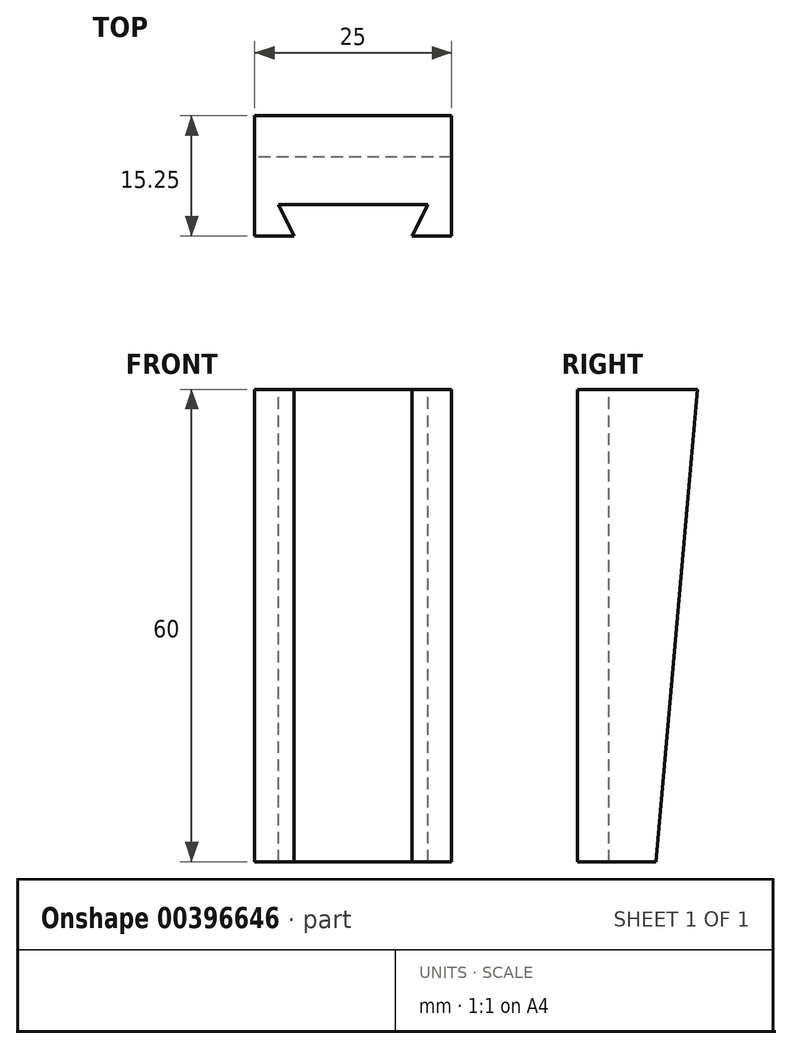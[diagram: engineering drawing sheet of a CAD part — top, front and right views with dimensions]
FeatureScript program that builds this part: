
annotation { "Feature Type Name" : "Feature", "Feature Type Description" : "" }
export const myFeature = defineFeature(function(context is Context, id is Id, definition is map)
    precondition{}
    {
        {
            assignVariable(context, id + "F0", {"name" : "height", "anyValue" : 60});
        }
        {
            assignVariable(context, id + "F1", {"name" : "width", "anyValue" : 25});
        }
        {
            var Q0;
            Q0=qCreatedBy(makeId("Top.planeOp"),FACE);
            var sketch = newSketch(context, id + "F2", { "sketchPlane" : qUnion([Q0])});
            skLineSegment(sketch, "E0.bottom", {"start": v(12.5, 10) * mm, "end": v(-12.5, 10) * mm});
            skLineSegment(sketch, "E0.top", {"start": v(12.5, 0) * mm, "end": v(-12.5, 0) * mm});
            skLineSegment(sketch, "E0.left", {"start": v(12.5, 10) * mm, "end": v(12.5, 0) * mm});
            skLineSegment(sketch, "E0.right", {"start": v(-12.5, 10) * mm, "end": v(-12.5, 0) * mm});
            skSolve(sketch);
        }
        {
            var Q0;
            Q0=makeQuery(id+"F2.imprint","IMPRINT",FACE,{"disambiguationData":[TD([[makeQuery(id+"F2.imprint","IMPRINT",EDGE,{"derivedFrom":sQuery(id+"F2.wireOp",EDGE,"E0.bottom")}),1.0]])]});
            extrude(context, id + "F3", {"entities" : qUnion([Q0]), "depth" : (getVariable(context, 'height')) * mm});
        }
        {
            var Q0;
            Q0=qCreatedBy(makeId("Right.planeOp"),FACE);
            var sketch = newSketch(context, id + "F4", { "sketchPlane" : qUnion([Q0])});
            skLineSegment(sketch, "E1", {"start": v(10, 0) * mm, "end": v(10, 60) * mm});
            skLineSegment(sketch, "E2", {"start": v(10, 60) * mm, "end": v(15.25, 60) * mm});
            skLineSegment(sketch, "E3", {"start": v(15.25, 60) * mm, "end": v(10, 0) * mm});
            skSolve(sketch);
        }
        {
            var Q0;
            Q0 = qSketchRegion(id + "F4", true);
            extrude(context, id + "F5", {"entities" : qUnion([Q0]), "operationType" : NewBodyOperationType.ADD, "endBound" : BoundingType.SYMMETRIC, "depth" : (getVariable(context, 'width')) * mm});
        }
        {
            var Q0;
            Q0=makeQuery(id+"F3.opExtrude","CAP_FACE",FACE,{"disambiguationData":[OSD([sQuery(id+"F2.wireOp",EDGE,"E0.bottom"),sQuery(id+"F2.wireOp",EDGE,"E0.top"),sQuery(id+"F2.wireOp",EDGE,"E0.left"),sQuery(id+"F2.wireOp",EDGE,"E0.right")])],"isStart":true});
            var sketch = newSketch(context, id + "F6", { "sketchPlane" : qUnion([Q0])});
            skLineSegment(sketch, "E4.bottom", {"start": v(7.5, 0) * mm, "end": v(-7.5, 0) * mm, "construction": true});
            skLineSegment(sketch, "E4.top", {"start": v(7.5, -4) * mm, "end": v(-7.5, -4) * mm, "construction": true});
            skLineSegment(sketch, "E4.left", {"start": v(7.5, 0) * mm, "end": v(7.5, -4) * mm, "construction": true});
            skLineSegment(sketch, "E4.right", {"start": v(-7.5, 0) * mm, "end": v(-7.5, -4) * mm, "construction": true});
            skLineSegment(sketch, "E5", {"start": v(-7.5, -4) * mm, "end": v(-9.5, -4) * mm, "construction": true});
            skLineSegment(sketch, "E6", {"start": v(7.5, -4) * mm, "end": v(9.5, -4) * mm, "construction": true});
            skLineSegment(sketch, "E7", {"start": v(-7.5, 0) * mm, "end": v(-9.5, -4) * mm});
            skLineSegment(sketch, "E8", {"start": v(-9.5, -4) * mm, "end": v(9.5, -4) * mm});
            skLineSegment(sketch, "E9", {"start": v(9.5, -4) * mm, "end": v(7.5, 0) * mm});
            skLineSegment(sketch, "E10", {"start": v(7.5, 0) * mm, "end": v(-7.5, 0) * mm});
            skSolve(sketch);
        }
        {
            var Q0;
            Q0=makeQuery(id+"F5.boolean.opBoolean","MERGE",FACE,{"derivedFrom":[makeQuery(id+"F3.opExtrude","CAP_FACE",FACE,{"disambiguationData":[OSD([sQuery(id+"F2.wireOp",EDGE,"E0.bottom"),sQuery(id+"F2.wireOp",EDGE,"E0.top"),sQuery(id+"F2.wireOp",EDGE,"E0.left"),sQuery(id+"F2.wireOp",EDGE,"E0.right")])],"isStart":false}),makeQuery(id+"F5.opExtrude","SWEPT_FACE",FACE,{"disambiguationData":[OSD([sQuery(id+"F4.wireOp",EDGE,"E2")])]})]});
            var sketch = newSketch(context, id + "F7", { "sketchPlane" : qUnion([Q0])});
            skPoint(sketch, "E11", {"position": v(-7.5, 0) * mm});
            skPoint(sketch, "E12", {"position": v(-9.5, 4) * mm});
            skPoint(sketch, "E13", {"position": v(9.5, 4) * mm});
            skPoint(sketch, "E14", {"position": v(7.5, 0) * mm});
            skLineSegment(sketch, "E15", {"start": v(-7.5, 0) * mm, "end": v(-9.5, 4) * mm});
            skLineSegment(sketch, "E16", {"start": v(-9.5, 4) * mm, "end": v(9.5, 4) * mm});
            skLineSegment(sketch, "E17", {"start": v(9.5, 4) * mm, "end": v(7.5, 0) * mm});
            skLineSegment(sketch, "E18", {"start": v(7.5, 0) * mm, "end": v(-7.5, 0) * mm});
            skSolve(sketch);
        }
        {
            var Q0;
            Q0 = qSketchRegion(id + "F7", true);
            extrude(context, id + "F8", {"entities" : qUnion([Q0]), "operationType" : NewBodyOperationType.REMOVE, "endBound" : BoundingType.UP_TO_NEXT, "oppositeDirection" : true, "depth" : 58.5 * mm});
        }
    });
